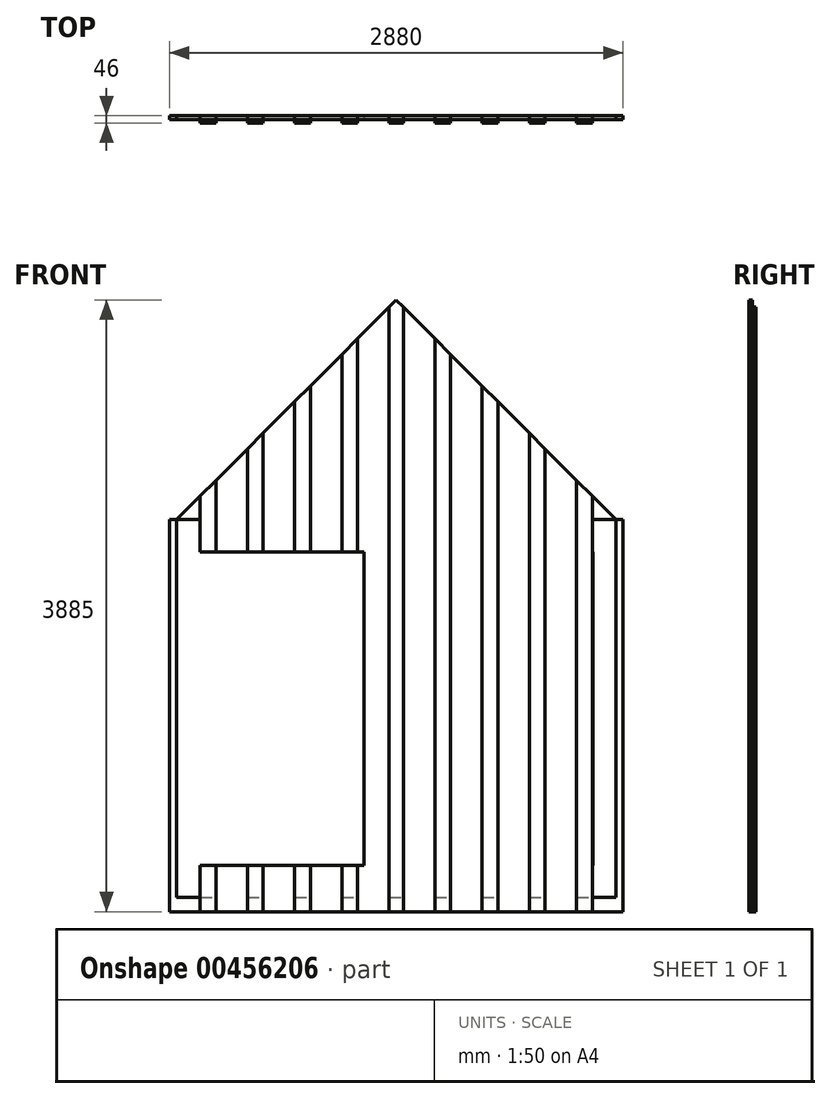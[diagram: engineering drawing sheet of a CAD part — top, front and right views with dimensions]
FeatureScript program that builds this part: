
annotation { "Feature Type Name" : "Feature", "Feature Type Description" : "" }
export const myFeature = defineFeature(function(context is Context, id is Id, definition is map)
    precondition{}
    {
        {
            var Q0;
            Q0=qCreatedBy(makeId("Front.planeOp"),FACE);
            var sketch = newSketch(context, id + "F0", { "sketchPlane" : qUnion([Q0])});
            skLineSegment(sketch, "E0.bottom", {"start": v(-2340, 1043.57) * mm, "end": v(450, 1043.57) * mm});
            skLineSegment(sketch, "E0.top", {"start": v(-2340, -1356.43) * mm, "end": v(450, -1356.43) * mm});
            skLineSegment(sketch, "E0.left", {"start": v(-2340, 1043.57) * mm, "end": v(-2340, -1356.43) * mm});
            skLineSegment(sketch, "E0.right", {"start": v(450, 1043.57) * mm, "end": v(450, -1356.43) * mm});
            skLineSegment(sketch, "E1", {"start": v(-2340, 1043.57) * mm, "end": v(-945, 2438.57) * mm});
            skPoint(sketch, "E1.endSnap0", {"position": v(-945, 1043.57) * mm});
            skLineSegment(sketch, "E2", {"start": v(-945, 2438.57) * mm, "end": v(450, 1043.57) * mm});
            skLineSegment(sketch, "E3.0", {"start": v(-945, 2233.5) * mm, "end": v(305, 983.5) * mm});
            skLineSegment(sketch, "E3.1", {"start": v(-2195, 983.5) * mm, "end": v(-945, 2233.5) * mm});
            skLineSegment(sketch, "E3.2", {"start": v(305, 983.5) * mm, "end": v(305, -1211.43) * mm});
            skLineSegment(sketch, "E3.3", {"start": v(-2195, -1211.43) * mm, "end": v(305, -1211.43) * mm});
            skLineSegment(sketch, "E3.4", {"start": v(-2195, 983.5) * mm, "end": v(-2195, -1211.43) * mm});
            skLineSegment(sketch, "E4.bottom", {"start": v(-2195, 983.5) * mm, "end": v(305, 983.5) * mm});
            skLineSegment(sketch, "E4.top", {"start": v(-2195, 838.5) * mm, "end": v(305, 838.5) * mm});
            skLineSegment(sketch, "E4.left", {"start": v(-2195, 983.5) * mm, "end": v(-2195, 838.5) * mm});
            skLineSegment(sketch, "E4.right", {"start": v(305, 983.5) * mm, "end": v(305, 838.5) * mm});
            skLineSegment(sketch, "E5", {"start": v(-2195, -1152) * mm, "end": v(305, -1152) * mm});
            skLineSegment(sketch, "E6", {"start": v(-2150, 838.5) * mm, "end": v(-2150, -1152) * mm});
            skLineSegment(sketch, "E7", {"start": v(260, 838.5) * mm, "end": v(260, -1152) * mm});
            skLineSegment(sketch, "E8.top", {"start": v(-2340, -1446.43) * mm, "end": v(450, -1446.43) * mm});
            skLineSegment(sketch, "E8.left", {"start": v(-2340, -1356.43) * mm, "end": v(-2340, -1446.43) * mm});
            skLineSegment(sketch, "E8.right", {"start": v(450, -1356.43) * mm, "end": v(450, -1446.43) * mm});
            skLineSegment(sketch, "E9", {"start": v(300, 988.5) * mm, "end": v(300, -1446.43) * mm});
            skLineSegment(sketch, "E10", {"start": v(200, 1088.5) * mm, "end": v(200, -1446.43) * mm});
            skLineSegment(sketch, "E11", {"start": v(0, 1288.5) * mm, "end": v(0, -1446.43) * mm});
            skLineSegment(sketch, "E12", {"start": v(-100, 1388.5) * mm, "end": v(-100, -1446.43) * mm});
            skLineSegment(sketch, "E13", {"start": v(-100, 1388.5) * mm, "end": v(-100, 1593.57) * mm});
            skLineSegment(sketch, "E14", {"start": v(0, 1288.5) * mm, "end": v(0, 1493.57) * mm});
            skLineSegment(sketch, "E15", {"start": v(200, 1088.5) * mm, "end": v(200, 1293.57) * mm});
            skLineSegment(sketch, "E16", {"start": v(300, 988.5) * mm, "end": v(300, 1193.57) * mm});
            skLineSegment(sketch, "E17", {"start": v(-300, 1793.57) * mm, "end": v(-300, -1446.43) * mm});
            skLineSegment(sketch, "E18", {"start": v(-400, 1893.57) * mm, "end": v(-400, -1446.43) * mm});
            skLineSegment(sketch, "E19", {"start": v(-600, 2093.57) * mm, "end": v(-600, -1446.43) * mm});
            skLineSegment(sketch, "E20", {"start": v(-700, 2193.57) * mm, "end": v(-700, -1446.43) * mm});
            skLineSegment(sketch, "E21", {"start": v(-900, 2393.57) * mm, "end": v(-900, -1446.43) * mm});
            skPoint(sketch, "E21.endSnap0", {"position": v(-945, -1446.43) * mm});
            skLineSegment(sketch, "E22", {"start": v(-945, 2438.57) * mm, "end": v(-945, 1939.82) * mm, "construction": true});
            skLineSegment(sketch, "E23.bottom", {"start": v(-2150, 838.5) * mm, "end": v(-1150, 838.5) * mm});
            skLineSegment(sketch, "E23.top", {"start": v(-2150, -1152) * mm, "end": v(-1150, -1152) * mm});
            skLineSegment(sketch, "E23.right", {"start": v(-1150, 838.5) * mm, "end": v(-1150, -1152) * mm});
            skLineSegment(sketch, "E24", {"start": v(-2150, 793.5) * mm, "end": v(-1150, 793.5) * mm});
            skLineSegment(sketch, "E25", {"start": v(-2150, -1107) * mm, "end": v(-1150, -1107) * mm});
            skLineSegment(sketch, "E26", {"start": v(-2105, 793.5) * mm, "end": v(-2105, -1107) * mm});
            skLineSegment(sketch, "E27", {"start": v(-1195, 793.5) * mm, "end": v(-1195, -1107) * mm});
            skLineSegment(sketch, "E28.MirrorCS", {"start": v(-2190, 988.5) * mm, "end": v(-2190, -1446.43) * mm});
            skLineSegment(sketch, "E29.MirrorCS", {"start": v(-2190, 988.5) * mm, "end": v(-2190, 1193.57) * mm});
            skLineSegment(sketch, "E30.MirrorCS", {"start": v(-2090, 1088.5) * mm, "end": v(-2090, -1446.43) * mm});
            skLineSegment(sketch, "E31.MirrorCS", {"start": v(-2090, 1088.5) * mm, "end": v(-2090, 1293.57) * mm});
            skLineSegment(sketch, "E32.MirrorCS", {"start": v(-1890, 1288.5) * mm, "end": v(-1890, 1493.57) * mm});
            skLineSegment(sketch, "E33.MirrorCS", {"start": v(-1790, 1388.5) * mm, "end": v(-1790, 1593.57) * mm});
            skLineSegment(sketch, "E34.MirrorCS", {"start": v(-1890, 1288.5) * mm, "end": v(-1890, -1446.43) * mm});
            skLineSegment(sketch, "E35.MirrorCS", {"start": v(-1790, 1388.5) * mm, "end": v(-1790, -1446.43) * mm});
            skLineSegment(sketch, "E36.MirrorCS", {"start": v(-1590, 1793.57) * mm, "end": v(-1590, -1446.43) * mm});
            skLineSegment(sketch, "E37.MirrorCS", {"start": v(-1490, 1893.57) * mm, "end": v(-1490, -1446.43) * mm});
            skLineSegment(sketch, "E38.MirrorCS", {"start": v(-1290, 2093.57) * mm, "end": v(-1290, -1446.43) * mm});
            skLineSegment(sketch, "E39.MirrorCS", {"start": v(-990, 2393.57) * mm, "end": v(-990, -1446.43) * mm});
            skLineSegment(sketch, "E40.MirrorCS", {"start": v(-1190, 2193.57) * mm, "end": v(-1190, -1446.43) * mm});
            skLineSegment(sketch, "E41.bottom", {"start": v(450, 1043.57) * mm, "end": v(495, 1043.57) * mm});
            skLineSegment(sketch, "E41.top", {"start": v(450, -1446.43) * mm, "end": v(495, -1446.43) * mm});
            skLineSegment(sketch, "E41.left", {"start": v(450, 1043.57) * mm, "end": v(450, -1446.43) * mm});
            skLineSegment(sketch, "E41.right", {"start": v(495, 1043.57) * mm, "end": v(495, -1446.43) * mm});
            skLineSegment(sketch, "E42.bottom", {"start": v(-2340, 1043.57) * mm, "end": v(-2385, 1043.57) * mm});
            skLineSegment(sketch, "E42.top", {"start": v(-2340, -1446.43) * mm, "end": v(-2385, -1446.43) * mm});
            skLineSegment(sketch, "E42.left", {"start": v(-2340, 1043.57) * mm, "end": v(-2340, -1446.43) * mm});
            skLineSegment(sketch, "E42.right", {"start": v(-2385, 1043.57) * mm, "end": v(-2385, -1446.43) * mm});
            skSolve(sketch);
        }
        {
            var Q0;
            {var subQ3=sQuery(id+"F0.wireOp",EDGE,"E41.bottom");Q0=makeQuery(id+"F0.imprint","IMPRINT",FACE,{"disambiguationData":[TD([[makeQuery(id+"F0.imprint","IMPRINT",EDGE,{"derivedFrom":subQ3}),-1.0]])]});}
            var Q1;
            {var subQ9=sQuery(id+"F0.wireOp",EDGE,"E4.right");Q1=makeQuery(id+"F0.imprint","IMPRINT",FACE,{"disambiguationData":[TD([[makeQuery(id+"F0.imprint","IMPRINT",EDGE,{"derivedFrom":subQ9}),1.0]])]});}
            var Q2;
            {var subQ1=sQuery(id+"F0.wireOp",EDGE,"E3.2");var subQ3=sQuery(id+"F0.wireOp",EDGE,"E5");var subQ4=makeQuery(id+"F0.imprint","INTERSECT",VERTEX,{"derivedFrom":[subQ1,subQ3]});Q2=makeQuery(id+"F0.imprint","IMPRINT",FACE,{"disambiguationData":[TD([[makeQuery(id+"F0.imprint","IMPRINT",EDGE,{"disambiguationData":[TD([[subQ4,1.0]])],"derivedFrom":subQ3}),1.0]])]});}
            var Q3;
            {var subQ0=sQuery(id+"F0.wireOp",EDGE,"E2");var subQ3=sQuery(id+"F0.wireOp",EDGE,"E16");var subQ5=makeQuery(id+"F0.imprint","INTERSECT",VERTEX,{"derivedFrom":[subQ0,subQ3]});Q3=makeQuery(id+"F0.imprint","IMPRINT",FACE,{"disambiguationData":[TD([[makeQuery(id+"F0.imprint","IMPRINT",EDGE,{"disambiguationData":[TD([[subQ5,1.0]])],"derivedFrom":subQ3}),-1.0]])]});}
            var Q4;
            {var subQ0=sQuery(id+"F0.wireOp",EDGE,"E14");Q4=makeQuery(id+"F0.imprint","IMPRINT",FACE,{"disambiguationData":[TD([[makeQuery(id+"F0.imprint","IMPRINT",EDGE,{"derivedFrom":subQ0}),-1.0]])]});}
            var Q5;
            {var subQ0=sQuery(id+"F0.wireOp",EDGE,"E11");var subQ1=sQuery(id+"F0.wireOp",EDGE,"E0.bottom");var subQ2=makeQuery(id+"F0.imprint","INTERSECT",VERTEX,{"derivedFrom":[subQ1,subQ0]});Q5=makeQuery(id+"F0.imprint","IMPRINT",FACE,{"disambiguationData":[TD([[makeQuery(id+"F0.imprint","IMPRINT",EDGE,{"disambiguationData":[TD([[subQ2,-1.0]])],"derivedFrom":subQ1}),1.0]])]});}
            var Q6;
            {var subQ0=sQuery(id+"F0.wireOp",EDGE,"E11");var subQ1=sQuery(id+"F0.wireOp",EDGE,"E0.bottom");var subQ2=makeQuery(id+"F0.imprint","INTERSECT",VERTEX,{"derivedFrom":[subQ1,subQ0]});Q6=makeQuery(id+"F0.imprint","IMPRINT",FACE,{"disambiguationData":[TD([[makeQuery(id+"F0.imprint","IMPRINT",EDGE,{"disambiguationData":[TD([[subQ2,-1.0]])],"derivedFrom":subQ1}),-1.0]])]});}
            var Q7;
            {var subQ0=sQuery(id+"F0.wireOp",EDGE,"E11");var subQ1=sQuery(id+"F0.wireOp",EDGE,"E4.bottom");var subQ2=makeQuery(id+"F0.imprint","INTERSECT",VERTEX,{"derivedFrom":[subQ1,subQ0]});Q7=makeQuery(id+"F0.imprint","IMPRINT",FACE,{"disambiguationData":[TD([[makeQuery(id+"F0.imprint","IMPRINT",EDGE,{"disambiguationData":[TD([[subQ2,-1.0]])],"derivedFrom":subQ1}),-1.0]])]});}
            var Q8;
            {var subQ0=sQuery(id+"F0.wireOp",EDGE,"E11");var subQ1=sQuery(id+"F0.wireOp",EDGE,"E4.top");var subQ2=makeQuery(id+"F0.imprint","INTERSECT",VERTEX,{"derivedFrom":[subQ1,subQ0]});Q8=makeQuery(id+"F0.imprint","IMPRINT",FACE,{"disambiguationData":[TD([[makeQuery(id+"F0.imprint","IMPRINT",EDGE,{"disambiguationData":[TD([[subQ2,-1.0]])],"derivedFrom":subQ1}),-1.0]])]});}
            var Q9;
            {var subQ0=sQuery(id+"F0.wireOp",EDGE,"E11");var subQ1=sQuery(id+"F0.wireOp",EDGE,"E3.3");var subQ2=makeQuery(id+"F0.imprint","INTERSECT",VERTEX,{"derivedFrom":[subQ1,subQ0]});Q9=makeQuery(id+"F0.imprint","IMPRINT",FACE,{"disambiguationData":[TD([[makeQuery(id+"F0.imprint","IMPRINT",EDGE,{"disambiguationData":[TD([[subQ2,-1.0]])],"derivedFrom":subQ1}),1.0]])]});}
            var Q10;
            {var subQ0=sQuery(id+"F0.wireOp",EDGE,"E11");var subQ1=sQuery(id+"F0.wireOp",EDGE,"E3.3");var subQ2=makeQuery(id+"F0.imprint","INTERSECT",VERTEX,{"derivedFrom":[subQ1,subQ0]});Q10=makeQuery(id+"F0.imprint","IMPRINT",FACE,{"disambiguationData":[TD([[makeQuery(id+"F0.imprint","IMPRINT",EDGE,{"disambiguationData":[TD([[subQ2,-1.0]])],"derivedFrom":subQ1}),-1.0]])]});}
            var Q11;
            {var subQ0=sQuery(id+"F0.wireOp",EDGE,"E11");var subQ1=sQuery(id+"F0.wireOp",EDGE,"E0.top");var subQ2=makeQuery(id+"F0.imprint","INTERSECT",VERTEX,{"derivedFrom":[subQ1,subQ0]});Q11=makeQuery(id+"F0.imprint","IMPRINT",FACE,{"disambiguationData":[TD([[makeQuery(id+"F0.imprint","IMPRINT",EDGE,{"disambiguationData":[TD([[subQ2,-1.0]])],"derivedFrom":subQ1}),-1.0]])]});}
            var Q12;
            {var subQ0=sQuery(id+"F0.wireOp",EDGE,"E17");var subQ1=sQuery(id+"F0.wireOp",EDGE,"E0.top");var subQ2=makeQuery(id+"F0.imprint","INTERSECT",VERTEX,{"derivedFrom":[subQ1,subQ0]});Q12=makeQuery(id+"F0.imprint","IMPRINT",FACE,{"disambiguationData":[TD([[makeQuery(id+"F0.imprint","IMPRINT",EDGE,{"disambiguationData":[TD([[subQ2,-1.0]])],"derivedFrom":subQ1}),-1.0]])]});}
            var Q13;
            {var subQ0=sQuery(id+"F0.wireOp",EDGE,"E17");var subQ1=sQuery(id+"F0.wireOp",EDGE,"E3.3");var subQ2=makeQuery(id+"F0.imprint","INTERSECT",VERTEX,{"derivedFrom":[subQ1,subQ0]});Q13=makeQuery(id+"F0.imprint","IMPRINT",FACE,{"disambiguationData":[TD([[makeQuery(id+"F0.imprint","IMPRINT",EDGE,{"disambiguationData":[TD([[subQ2,-1.0]])],"derivedFrom":subQ1}),-1.0]])]});}
            var Q14;
            {var subQ0=sQuery(id+"F0.wireOp",EDGE,"E17");var subQ1=sQuery(id+"F0.wireOp",EDGE,"E3.3");var subQ2=makeQuery(id+"F0.imprint","INTERSECT",VERTEX,{"derivedFrom":[subQ1,subQ0]});Q14=makeQuery(id+"F0.imprint","IMPRINT",FACE,{"disambiguationData":[TD([[makeQuery(id+"F0.imprint","IMPRINT",EDGE,{"disambiguationData":[TD([[subQ2,-1.0]])],"derivedFrom":subQ1}),1.0]])]});}
            var Q15;
            {var subQ0=sQuery(id+"F0.wireOp",EDGE,"E17");var subQ1=sQuery(id+"F0.wireOp",EDGE,"E4.top");var subQ2=makeQuery(id+"F0.imprint","INTERSECT",VERTEX,{"derivedFrom":[subQ1,subQ0]});Q15=makeQuery(id+"F0.imprint","IMPRINT",FACE,{"disambiguationData":[TD([[makeQuery(id+"F0.imprint","IMPRINT",EDGE,{"disambiguationData":[TD([[subQ2,-1.0]])],"derivedFrom":subQ1}),-1.0]])]});}
            var Q16;
            {var subQ0=sQuery(id+"F0.wireOp",EDGE,"E17");var subQ1=sQuery(id+"F0.wireOp",EDGE,"E4.bottom");var subQ2=makeQuery(id+"F0.imprint","INTERSECT",VERTEX,{"derivedFrom":[subQ1,subQ0]});Q16=makeQuery(id+"F0.imprint","IMPRINT",FACE,{"disambiguationData":[TD([[makeQuery(id+"F0.imprint","IMPRINT",EDGE,{"disambiguationData":[TD([[subQ2,-1.0]])],"derivedFrom":subQ1}),-1.0]])]});}
            var Q17;
            {var subQ0=sQuery(id+"F0.wireOp",EDGE,"E17");var subQ1=sQuery(id+"F0.wireOp",EDGE,"E0.bottom");var subQ2=makeQuery(id+"F0.imprint","INTERSECT",VERTEX,{"derivedFrom":[subQ1,subQ0]});Q17=makeQuery(id+"F0.imprint","IMPRINT",FACE,{"disambiguationData":[TD([[makeQuery(id+"F0.imprint","IMPRINT",EDGE,{"disambiguationData":[TD([[subQ2,-1.0]])],"derivedFrom":subQ1}),-1.0]])]});}
            var Q18;
            {var subQ0=sQuery(id+"F0.wireOp",EDGE,"E17");var subQ1=sQuery(id+"F0.wireOp",EDGE,"E0.bottom");var subQ2=makeQuery(id+"F0.imprint","INTERSECT",VERTEX,{"derivedFrom":[subQ1,subQ0]});Q18=makeQuery(id+"F0.imprint","IMPRINT",FACE,{"disambiguationData":[TD([[makeQuery(id+"F0.imprint","IMPRINT",EDGE,{"disambiguationData":[TD([[subQ2,-1.0]])],"derivedFrom":subQ1}),1.0]])]});}
            var Q19;
            {var subQ0=sQuery(id+"F0.wireOp",EDGE,"E13");Q19=makeQuery(id+"F0.imprint","IMPRINT",FACE,{"disambiguationData":[TD([[makeQuery(id+"F0.imprint","IMPRINT",EDGE,{"derivedFrom":subQ0}),1.0]])]});}
            var Q20;
            {var subQ0=sQuery(id+"F0.wireOp",EDGE,"E18");var subQ1=sQuery(id+"F0.wireOp",EDGE,"E2");var subQ2=makeQuery(id+"F0.imprint","INTERSECT",VERTEX,{"derivedFrom":[subQ1,subQ0]});Q20=makeQuery(id+"F0.imprint","IMPRINT",FACE,{"disambiguationData":[TD([[makeQuery(id+"F0.imprint","IMPRINT",EDGE,{"disambiguationData":[TD([[subQ2,1.0]])],"derivedFrom":subQ1}),-1.0]])]});}
            var Q21;
            {var subQ0=sQuery(id+"F0.wireOp",EDGE,"E19");var subQ1=sQuery(id+"F0.wireOp",EDGE,"E0.bottom");var subQ2=makeQuery(id+"F0.imprint","INTERSECT",VERTEX,{"derivedFrom":[subQ1,subQ0]});Q21=makeQuery(id+"F0.imprint","IMPRINT",FACE,{"disambiguationData":[TD([[makeQuery(id+"F0.imprint","IMPRINT",EDGE,{"disambiguationData":[TD([[subQ2,-1.0]])],"derivedFrom":subQ1}),1.0]])]});}
            var Q22;
            {var subQ0=sQuery(id+"F0.wireOp",EDGE,"E19");var subQ1=sQuery(id+"F0.wireOp",EDGE,"E0.bottom");var subQ2=makeQuery(id+"F0.imprint","INTERSECT",VERTEX,{"derivedFrom":[subQ1,subQ0]});Q22=makeQuery(id+"F0.imprint","IMPRINT",FACE,{"disambiguationData":[TD([[makeQuery(id+"F0.imprint","IMPRINT",EDGE,{"disambiguationData":[TD([[subQ2,-1.0]])],"derivedFrom":subQ1}),-1.0]])]});}
            var Q23;
            {var subQ0=sQuery(id+"F0.wireOp",EDGE,"E19");var subQ1=sQuery(id+"F0.wireOp",EDGE,"E4.bottom");var subQ2=makeQuery(id+"F0.imprint","INTERSECT",VERTEX,{"derivedFrom":[subQ1,subQ0]});Q23=makeQuery(id+"F0.imprint","IMPRINT",FACE,{"disambiguationData":[TD([[makeQuery(id+"F0.imprint","IMPRINT",EDGE,{"disambiguationData":[TD([[subQ2,-1.0]])],"derivedFrom":subQ1}),-1.0]])]});}
            var Q24;
            {var subQ0=sQuery(id+"F0.wireOp",EDGE,"E19");var subQ1=sQuery(id+"F0.wireOp",EDGE,"E4.top");var subQ2=makeQuery(id+"F0.imprint","INTERSECT",VERTEX,{"derivedFrom":[subQ1,subQ0]});Q24=makeQuery(id+"F0.imprint","IMPRINT",FACE,{"disambiguationData":[TD([[makeQuery(id+"F0.imprint","IMPRINT",EDGE,{"disambiguationData":[TD([[subQ2,-1.0]])],"derivedFrom":subQ1}),-1.0]])]});}
            var Q25;
            {var subQ0=sQuery(id+"F0.wireOp",EDGE,"E19");var subQ1=sQuery(id+"F0.wireOp",EDGE,"E3.3");var subQ2=makeQuery(id+"F0.imprint","INTERSECT",VERTEX,{"derivedFrom":[subQ1,subQ0]});Q25=makeQuery(id+"F0.imprint","IMPRINT",FACE,{"disambiguationData":[TD([[makeQuery(id+"F0.imprint","IMPRINT",EDGE,{"disambiguationData":[TD([[subQ2,-1.0]])],"derivedFrom":subQ1}),1.0]])]});}
            var Q26;
            {var subQ0=sQuery(id+"F0.wireOp",EDGE,"E19");var subQ1=sQuery(id+"F0.wireOp",EDGE,"E3.3");var subQ2=makeQuery(id+"F0.imprint","INTERSECT",VERTEX,{"derivedFrom":[subQ1,subQ0]});Q26=makeQuery(id+"F0.imprint","IMPRINT",FACE,{"disambiguationData":[TD([[makeQuery(id+"F0.imprint","IMPRINT",EDGE,{"disambiguationData":[TD([[subQ2,-1.0]])],"derivedFrom":subQ1}),-1.0]])]});}
            var Q27;
            {var subQ0=sQuery(id+"F0.wireOp",EDGE,"E19");var subQ1=sQuery(id+"F0.wireOp",EDGE,"E0.top");var subQ2=makeQuery(id+"F0.imprint","INTERSECT",VERTEX,{"derivedFrom":[subQ1,subQ0]});Q27=makeQuery(id+"F0.imprint","IMPRINT",FACE,{"disambiguationData":[TD([[makeQuery(id+"F0.imprint","IMPRINT",EDGE,{"disambiguationData":[TD([[subQ2,-1.0]])],"derivedFrom":subQ1}),-1.0]])]});}
            var Q28;
            {var subQ0=sQuery(id+"F0.wireOp",EDGE,"E21");var subQ1=sQuery(id+"F0.wireOp",EDGE,"E0.top");var subQ2=makeQuery(id+"F0.imprint","INTERSECT",VERTEX,{"derivedFrom":[subQ1,subQ0]});Q28=makeQuery(id+"F0.imprint","IMPRINT",FACE,{"disambiguationData":[TD([[makeQuery(id+"F0.imprint","IMPRINT",EDGE,{"disambiguationData":[TD([[subQ2,-1.0]])],"derivedFrom":subQ1}),-1.0]])]});}
            var Q29;
            {var subQ0=sQuery(id+"F0.wireOp",EDGE,"E21");var subQ1=sQuery(id+"F0.wireOp",EDGE,"E3.3");var subQ2=makeQuery(id+"F0.imprint","INTERSECT",VERTEX,{"derivedFrom":[subQ1,subQ0]});Q29=makeQuery(id+"F0.imprint","IMPRINT",FACE,{"disambiguationData":[TD([[makeQuery(id+"F0.imprint","IMPRINT",EDGE,{"disambiguationData":[TD([[subQ2,-1.0]])],"derivedFrom":subQ1}),-1.0]])]});}
            var Q30;
            {var subQ0=sQuery(id+"F0.wireOp",EDGE,"E21");var subQ1=sQuery(id+"F0.wireOp",EDGE,"E3.3");var subQ2=makeQuery(id+"F0.imprint","INTERSECT",VERTEX,{"derivedFrom":[subQ1,subQ0]});Q30=makeQuery(id+"F0.imprint","IMPRINT",FACE,{"disambiguationData":[TD([[makeQuery(id+"F0.imprint","IMPRINT",EDGE,{"disambiguationData":[TD([[subQ2,-1.0]])],"derivedFrom":subQ1}),1.0]])]});}
            var Q31;
            {var subQ0=sQuery(id+"F0.wireOp",EDGE,"E21");var subQ1=sQuery(id+"F0.wireOp",EDGE,"E4.top");var subQ2=makeQuery(id+"F0.imprint","INTERSECT",VERTEX,{"derivedFrom":[subQ1,subQ0]});Q31=makeQuery(id+"F0.imprint","IMPRINT",FACE,{"disambiguationData":[TD([[makeQuery(id+"F0.imprint","IMPRINT",EDGE,{"disambiguationData":[TD([[subQ2,-1.0]])],"derivedFrom":subQ1}),-1.0]])]});}
            var Q32;
            {var subQ0=sQuery(id+"F0.wireOp",EDGE,"E21");var subQ1=sQuery(id+"F0.wireOp",EDGE,"E4.bottom");var subQ2=makeQuery(id+"F0.imprint","INTERSECT",VERTEX,{"derivedFrom":[subQ1,subQ0]});Q32=makeQuery(id+"F0.imprint","IMPRINT",FACE,{"disambiguationData":[TD([[makeQuery(id+"F0.imprint","IMPRINT",EDGE,{"disambiguationData":[TD([[subQ2,-1.0]])],"derivedFrom":subQ1}),-1.0]])]});}
            var Q33;
            {var subQ0=sQuery(id+"F0.wireOp",EDGE,"E21");var subQ1=sQuery(id+"F0.wireOp",EDGE,"E0.bottom");var subQ2=makeQuery(id+"F0.imprint","INTERSECT",VERTEX,{"derivedFrom":[subQ1,subQ0]});Q33=makeQuery(id+"F0.imprint","IMPRINT",FACE,{"disambiguationData":[TD([[makeQuery(id+"F0.imprint","IMPRINT",EDGE,{"disambiguationData":[TD([[subQ2,-1.0]])],"derivedFrom":subQ1}),-1.0]])]});}
            var Q34;
            {var subQ0=sQuery(id+"F0.wireOp",EDGE,"E21");var subQ1=sQuery(id+"F0.wireOp",EDGE,"E0.bottom");var subQ2=makeQuery(id+"F0.imprint","INTERSECT",VERTEX,{"derivedFrom":[subQ1,subQ0]});Q34=makeQuery(id+"F0.imprint","IMPRINT",FACE,{"disambiguationData":[TD([[makeQuery(id+"F0.imprint","IMPRINT",EDGE,{"disambiguationData":[TD([[subQ2,-1.0]])],"derivedFrom":subQ1}),1.0]])]});}
            var Q35;
            {var subQ0=sQuery(id+"F0.wireOp",EDGE,"E20");var subQ1=sQuery(id+"F0.wireOp",EDGE,"E2");var subQ2=makeQuery(id+"F0.imprint","INTERSECT",VERTEX,{"derivedFrom":[subQ1,subQ0]});Q35=makeQuery(id+"F0.imprint","IMPRINT",FACE,{"disambiguationData":[TD([[makeQuery(id+"F0.imprint","IMPRINT",EDGE,{"disambiguationData":[TD([[subQ2,1.0]])],"derivedFrom":subQ1}),-1.0]])]});}
            var Q36;
            {var subQ0=sQuery(id+"F0.wireOp",EDGE,"E39.MirrorCS");var subQ1=sQuery(id+"F0.wireOp",EDGE,"E1");var subQ2=makeQuery(id+"F0.imprint","INTERSECT",VERTEX,{"derivedFrom":[subQ1,subQ0]});Q36=makeQuery(id+"F0.imprint","IMPRINT",FACE,{"disambiguationData":[TD([[makeQuery(id+"F0.imprint","IMPRINT",EDGE,{"disambiguationData":[TD([[subQ2,1.0]])],"derivedFrom":subQ1}),-1.0]])]});}
            var Q37;
            {var subQ0=sQuery(id+"F0.wireOp",EDGE,"E40.MirrorCS");var subQ1=sQuery(id+"F0.wireOp",EDGE,"E0.bottom");var subQ2=makeQuery(id+"F0.imprint","INTERSECT",VERTEX,{"derivedFrom":[subQ1,subQ0]});Q37=makeQuery(id+"F0.imprint","IMPRINT",FACE,{"disambiguationData":[TD([[makeQuery(id+"F0.imprint","IMPRINT",EDGE,{"disambiguationData":[TD([[subQ2,-1.0]])],"derivedFrom":subQ1}),1.0]])]});}
            var Q38;
            {var subQ0=sQuery(id+"F0.wireOp",EDGE,"E40.MirrorCS");var subQ1=sQuery(id+"F0.wireOp",EDGE,"E0.bottom");var subQ2=makeQuery(id+"F0.imprint","INTERSECT",VERTEX,{"derivedFrom":[subQ1,subQ0]});Q38=makeQuery(id+"F0.imprint","IMPRINT",FACE,{"disambiguationData":[TD([[makeQuery(id+"F0.imprint","IMPRINT",EDGE,{"disambiguationData":[TD([[subQ2,-1.0]])],"derivedFrom":subQ1}),-1.0]])]});}
            var Q39;
            {var subQ1=sQuery(id+"F0.wireOp",EDGE,"E4.bottom");var subQ7=sQuery(id+"F0.wireOp",EDGE,"E40.MirrorCS");var subQ9=makeQuery(id+"F0.imprint","INTERSECT",VERTEX,{"derivedFrom":[subQ1,subQ7]});Q39=makeQuery(id+"F0.imprint","IMPRINT",FACE,{"disambiguationData":[TD([[makeQuery(id+"F0.imprint","IMPRINT",EDGE,{"disambiguationData":[TD([[subQ9,-1.0]])],"derivedFrom":subQ1}),-1.0]])]});}
            var Q40;
            {var subQ0=sQuery(id+"F0.wireOp",EDGE,"E23.right");var subQ1=makeQuery(id+"F0.imprint","INTERSECT",VERTEX,{"derivedFrom":[subQ0,sQuery(id+"F0.wireOp",EDGE,"E24")]});Q40=makeQuery(id+"F0.imprint","IMPRINT",FACE,{"disambiguationData":[TD([[makeQuery(id+"F0.imprint","IMPRINT",EDGE,{"disambiguationData":[TD([[subQ1,-1.0]])],"derivedFrom":subQ0}),1.0]])]});}
            var Q41;
            {var subQ0=sQuery(id+"F0.wireOp",EDGE,"E40.MirrorCS");var subQ1=sQuery(id+"F0.wireOp",EDGE,"E3.3");var subQ2=makeQuery(id+"F0.imprint","INTERSECT",VERTEX,{"derivedFrom":[subQ1,subQ0]});Q41=makeQuery(id+"F0.imprint","IMPRINT",FACE,{"disambiguationData":[TD([[makeQuery(id+"F0.imprint","IMPRINT",EDGE,{"disambiguationData":[TD([[subQ2,-1.0]])],"derivedFrom":subQ1}),-1.0]])]});}
            var Q42;
            {var subQ3=sQuery(id+"F0.wireOp",EDGE,"E40.MirrorCS");var subQ6=sQuery(id+"F0.wireOp",EDGE,"E3.3");var subQ9=makeQuery(id+"F0.imprint","INTERSECT",VERTEX,{"derivedFrom":[subQ6,subQ3]});Q42=makeQuery(id+"F0.imprint","IMPRINT",FACE,{"disambiguationData":[TD([[makeQuery(id+"F0.imprint","IMPRINT",EDGE,{"disambiguationData":[TD([[subQ9,-1.0]])],"derivedFrom":subQ6}),1.0]])]});}
            var Q43;
            {var subQ0=sQuery(id+"F0.wireOp",EDGE,"E37.MirrorCS");var subQ1=sQuery(id+"F0.wireOp",EDGE,"E3.3");var subQ2=makeQuery(id+"F0.imprint","INTERSECT",VERTEX,{"derivedFrom":[subQ1,subQ0]});Q43=makeQuery(id+"F0.imprint","IMPRINT",FACE,{"disambiguationData":[TD([[makeQuery(id+"F0.imprint","IMPRINT",EDGE,{"disambiguationData":[TD([[subQ2,-1.0]])],"derivedFrom":subQ1}),-1.0]])]});}
            var Q44;
            {var subQ0=sQuery(id+"F0.wireOp",EDGE,"E37.MirrorCS");var subQ1=sQuery(id+"F0.wireOp",EDGE,"E3.3");var subQ2=makeQuery(id+"F0.imprint","INTERSECT",VERTEX,{"derivedFrom":[subQ1,subQ0]});Q44=makeQuery(id+"F0.imprint","IMPRINT",FACE,{"disambiguationData":[TD([[makeQuery(id+"F0.imprint","IMPRINT",EDGE,{"disambiguationData":[TD([[subQ2,-1.0]])],"derivedFrom":subQ1}),1.0]])]});}
            var Q45;
            {var subQ0=sQuery(id+"F0.wireOp",EDGE,"E40.MirrorCS");var subQ1=sQuery(id+"F0.wireOp",EDGE,"E0.top");var subQ2=makeQuery(id+"F0.imprint","INTERSECT",VERTEX,{"derivedFrom":[subQ1,subQ0]});Q45=makeQuery(id+"F0.imprint","IMPRINT",FACE,{"disambiguationData":[TD([[makeQuery(id+"F0.imprint","IMPRINT",EDGE,{"disambiguationData":[TD([[subQ2,-1.0]])],"derivedFrom":subQ1}),-1.0]])]});}
            var Q46;
            {var subQ0=sQuery(id+"F0.wireOp",EDGE,"E37.MirrorCS");var subQ1=sQuery(id+"F0.wireOp",EDGE,"E0.top");var subQ2=makeQuery(id+"F0.imprint","INTERSECT",VERTEX,{"derivedFrom":[subQ1,subQ0]});Q46=makeQuery(id+"F0.imprint","IMPRINT",FACE,{"disambiguationData":[TD([[makeQuery(id+"F0.imprint","IMPRINT",EDGE,{"disambiguationData":[TD([[subQ2,-1.0]])],"derivedFrom":subQ1}),-1.0]])]});}
            var Q47;
            {var subQ0=sQuery(id+"F0.wireOp",EDGE,"E35.MirrorCS");var subQ1=sQuery(id+"F0.wireOp",EDGE,"E0.top");var subQ2=makeQuery(id+"F0.imprint","INTERSECT",VERTEX,{"derivedFrom":[subQ1,subQ0]});Q47=makeQuery(id+"F0.imprint","IMPRINT",FACE,{"disambiguationData":[TD([[makeQuery(id+"F0.imprint","IMPRINT",EDGE,{"disambiguationData":[TD([[subQ2,-1.0]])],"derivedFrom":subQ1}),-1.0]])]});}
            var Q48;
            {var subQ0=sQuery(id+"F0.wireOp",EDGE,"E35.MirrorCS");var subQ1=sQuery(id+"F0.wireOp",EDGE,"E3.3");var subQ2=makeQuery(id+"F0.imprint","INTERSECT",VERTEX,{"derivedFrom":[subQ1,subQ0]});Q48=makeQuery(id+"F0.imprint","IMPRINT",FACE,{"disambiguationData":[TD([[makeQuery(id+"F0.imprint","IMPRINT",EDGE,{"disambiguationData":[TD([[subQ2,-1.0]])],"derivedFrom":subQ1}),-1.0]])]});}
            var Q49;
            {var subQ0=sQuery(id+"F0.wireOp",EDGE,"E35.MirrorCS");var subQ1=sQuery(id+"F0.wireOp",EDGE,"E3.3");var subQ2=makeQuery(id+"F0.imprint","INTERSECT",VERTEX,{"derivedFrom":[subQ1,subQ0]});Q49=makeQuery(id+"F0.imprint","IMPRINT",FACE,{"disambiguationData":[TD([[makeQuery(id+"F0.imprint","IMPRINT",EDGE,{"disambiguationData":[TD([[subQ2,-1.0]])],"derivedFrom":subQ1}),1.0]])]});}
            var Q50;
            {var subQ0=sQuery(id+"F0.wireOp",EDGE,"E30.MirrorCS");var subQ1=sQuery(id+"F0.wireOp",EDGE,"E0.top");var subQ2=makeQuery(id+"F0.imprint","INTERSECT",VERTEX,{"derivedFrom":[subQ1,subQ0]});Q50=makeQuery(id+"F0.imprint","IMPRINT",FACE,{"disambiguationData":[TD([[makeQuery(id+"F0.imprint","IMPRINT",EDGE,{"disambiguationData":[TD([[subQ2,-1.0]])],"derivedFrom":subQ1}),-1.0]])]});}
            var Q51;
            {var subQ0=sQuery(id+"F0.wireOp",EDGE,"E30.MirrorCS");var subQ1=sQuery(id+"F0.wireOp",EDGE,"E3.3");var subQ2=makeQuery(id+"F0.imprint","INTERSECT",VERTEX,{"derivedFrom":[subQ1,subQ0]});Q51=makeQuery(id+"F0.imprint","IMPRINT",FACE,{"disambiguationData":[TD([[makeQuery(id+"F0.imprint","IMPRINT",EDGE,{"disambiguationData":[TD([[subQ2,-1.0]])],"derivedFrom":subQ1}),-1.0]])]});}
            var Q52;
            {var subQ0=sQuery(id+"F0.wireOp",EDGE,"E30.MirrorCS");var subQ1=sQuery(id+"F0.wireOp",EDGE,"E3.3");var subQ2=makeQuery(id+"F0.imprint","INTERSECT",VERTEX,{"derivedFrom":[subQ1,subQ0]});Q52=makeQuery(id+"F0.imprint","IMPRINT",FACE,{"disambiguationData":[TD([[makeQuery(id+"F0.imprint","IMPRINT",EDGE,{"disambiguationData":[TD([[subQ2,-1.0]])],"derivedFrom":subQ1}),1.0]])]});}
            var Q53;
            {var subQ0=sQuery(id+"F0.wireOp",EDGE,"E42.left");var subQ1=sQuery(id+"F0.wireOp",EDGE,"E0.top");var subQ2=makeQuery(id+"F0.imprint","INTERSECT",VERTEX,{"derivedFrom":[subQ1,subQ0]});Q53=makeQuery(id+"F0.imprint","IMPRINT",FACE,{"disambiguationData":[TD([[makeQuery(id+"F0.imprint","IMPRINT",EDGE,{"disambiguationData":[TD([[subQ2,-1.0]])],"derivedFrom":subQ1}),-1.0]])]});}
            var Q54;
            {var subQ3=sQuery(id+"F0.wireOp",EDGE,"E42.bottom");Q54=makeQuery(id+"F0.imprint","IMPRINT",FACE,{"disambiguationData":[TD([[makeQuery(id+"F0.imprint","IMPRINT",EDGE,{"derivedFrom":subQ3}),1.0]])]});}
            var Q55;
            {var subQ0=sQuery(id+"F0.wireOp",EDGE,"E4.left");Q55=makeQuery(id+"F0.imprint","IMPRINT",FACE,{"disambiguationData":[TD([[makeQuery(id+"F0.imprint","IMPRINT",EDGE,{"derivedFrom":subQ0}),-1.0]])]});}
            var Q56;
            {var subQ0=sQuery(id+"F0.wireOp",EDGE,"E1");var subQ3=sQuery(id+"F0.wireOp",EDGE,"E29.MirrorCS");var subQ5=makeQuery(id+"F0.imprint","INTERSECT",VERTEX,{"derivedFrom":[subQ0,subQ3]});Q56=makeQuery(id+"F0.imprint","IMPRINT",FACE,{"disambiguationData":[TD([[makeQuery(id+"F0.imprint","IMPRINT",EDGE,{"disambiguationData":[TD([[subQ5,1.0]])],"derivedFrom":subQ3}),1.0]])]});}
            var Q57;
            {var subQ0=sQuery(id+"F0.wireOp",EDGE,"E31.MirrorCS");Q57=makeQuery(id+"F0.imprint","IMPRINT",FACE,{"disambiguationData":[TD([[makeQuery(id+"F0.imprint","IMPRINT",EDGE,{"derivedFrom":subQ0}),-1.0]])]});}
            var Q58;
            {var subQ0=sQuery(id+"F0.wireOp",EDGE,"E30.MirrorCS");var subQ1=sQuery(id+"F0.wireOp",EDGE,"E0.bottom");var subQ2=makeQuery(id+"F0.imprint","INTERSECT",VERTEX,{"derivedFrom":[subQ1,subQ0]});Q58=makeQuery(id+"F0.imprint","IMPRINT",FACE,{"disambiguationData":[TD([[makeQuery(id+"F0.imprint","IMPRINT",EDGE,{"disambiguationData":[TD([[subQ2,-1.0]])],"derivedFrom":subQ1}),1.0]])]});}
            var Q59;
            {var subQ0=sQuery(id+"F0.wireOp",EDGE,"E35.MirrorCS");var subQ1=sQuery(id+"F0.wireOp",EDGE,"E0.bottom");var subQ2=makeQuery(id+"F0.imprint","INTERSECT",VERTEX,{"derivedFrom":[subQ1,subQ0]});Q59=makeQuery(id+"F0.imprint","IMPRINT",FACE,{"disambiguationData":[TD([[makeQuery(id+"F0.imprint","IMPRINT",EDGE,{"disambiguationData":[TD([[subQ2,-1.0]])],"derivedFrom":subQ1}),1.0]])]});}
            var Q60;
            {var subQ0=sQuery(id+"F0.wireOp",EDGE,"E33.MirrorCS");Q60=makeQuery(id+"F0.imprint","IMPRINT",FACE,{"disambiguationData":[TD([[makeQuery(id+"F0.imprint","IMPRINT",EDGE,{"derivedFrom":subQ0}),-1.0]])]});}
            var Q61;
            {var subQ0=sQuery(id+"F0.wireOp",EDGE,"E37.MirrorCS");var subQ1=sQuery(id+"F0.wireOp",EDGE,"E0.bottom");var subQ2=makeQuery(id+"F0.imprint","INTERSECT",VERTEX,{"derivedFrom":[subQ1,subQ0]});Q61=makeQuery(id+"F0.imprint","IMPRINT",FACE,{"disambiguationData":[TD([[makeQuery(id+"F0.imprint","IMPRINT",EDGE,{"disambiguationData":[TD([[subQ2,-1.0]])],"derivedFrom":subQ1}),1.0]])]});}
            var Q62;
            {var subQ0=sQuery(id+"F0.wireOp",EDGE,"E37.MirrorCS");var subQ1=sQuery(id+"F0.wireOp",EDGE,"E1");var subQ2=makeQuery(id+"F0.imprint","INTERSECT",VERTEX,{"derivedFrom":[subQ1,subQ0]});Q62=makeQuery(id+"F0.imprint","IMPRINT",FACE,{"disambiguationData":[TD([[makeQuery(id+"F0.imprint","IMPRINT",EDGE,{"disambiguationData":[TD([[subQ2,-1.0]])],"derivedFrom":subQ1}),-1.0]])]});}
            var Q63;
            {var subQ0=sQuery(id+"F0.wireOp",EDGE,"E30.MirrorCS");var subQ1=sQuery(id+"F0.wireOp",EDGE,"E0.bottom");var subQ2=makeQuery(id+"F0.imprint","INTERSECT",VERTEX,{"derivedFrom":[subQ1,subQ0]});Q63=makeQuery(id+"F0.imprint","IMPRINT",FACE,{"disambiguationData":[TD([[makeQuery(id+"F0.imprint","IMPRINT",EDGE,{"disambiguationData":[TD([[subQ2,-1.0]])],"derivedFrom":subQ1}),-1.0]])]});}
            var Q64;
            {var subQ0=sQuery(id+"F0.wireOp",EDGE,"E30.MirrorCS");var subQ1=sQuery(id+"F0.wireOp",EDGE,"E4.bottom");var subQ2=makeQuery(id+"F0.imprint","INTERSECT",VERTEX,{"derivedFrom":[subQ1,subQ0]});Q64=makeQuery(id+"F0.imprint","IMPRINT",FACE,{"disambiguationData":[TD([[makeQuery(id+"F0.imprint","IMPRINT",EDGE,{"disambiguationData":[TD([[subQ2,-1.0]])],"derivedFrom":subQ1}),-1.0]])]});}
            var Q65;
            {var subQ0=sQuery(id+"F0.wireOp",EDGE,"E35.MirrorCS");var subQ1=sQuery(id+"F0.wireOp",EDGE,"E0.bottom");var subQ2=makeQuery(id+"F0.imprint","INTERSECT",VERTEX,{"derivedFrom":[subQ1,subQ0]});Q65=makeQuery(id+"F0.imprint","IMPRINT",FACE,{"disambiguationData":[TD([[makeQuery(id+"F0.imprint","IMPRINT",EDGE,{"disambiguationData":[TD([[subQ2,-1.0]])],"derivedFrom":subQ1}),-1.0]])]});}
            var Q66;
            {var subQ0=sQuery(id+"F0.wireOp",EDGE,"E35.MirrorCS");var subQ1=sQuery(id+"F0.wireOp",EDGE,"E4.bottom");var subQ2=makeQuery(id+"F0.imprint","INTERSECT",VERTEX,{"derivedFrom":[subQ1,subQ0]});Q66=makeQuery(id+"F0.imprint","IMPRINT",FACE,{"disambiguationData":[TD([[makeQuery(id+"F0.imprint","IMPRINT",EDGE,{"disambiguationData":[TD([[subQ2,-1.0]])],"derivedFrom":subQ1}),-1.0]])]});}
            var Q67;
            {var subQ0=sQuery(id+"F0.wireOp",EDGE,"E37.MirrorCS");var subQ1=sQuery(id+"F0.wireOp",EDGE,"E0.bottom");var subQ2=makeQuery(id+"F0.imprint","INTERSECT",VERTEX,{"derivedFrom":[subQ1,subQ0]});Q67=makeQuery(id+"F0.imprint","IMPRINT",FACE,{"disambiguationData":[TD([[makeQuery(id+"F0.imprint","IMPRINT",EDGE,{"disambiguationData":[TD([[subQ2,-1.0]])],"derivedFrom":subQ1}),-1.0]])]});}
            var Q68;
            {var subQ0=sQuery(id+"F0.wireOp",EDGE,"E37.MirrorCS");var subQ1=sQuery(id+"F0.wireOp",EDGE,"E4.bottom");var subQ2=makeQuery(id+"F0.imprint","INTERSECT",VERTEX,{"derivedFrom":[subQ1,subQ0]});Q68=makeQuery(id+"F0.imprint","IMPRINT",FACE,{"disambiguationData":[TD([[makeQuery(id+"F0.imprint","IMPRINT",EDGE,{"disambiguationData":[TD([[subQ2,-1.0]])],"derivedFrom":subQ1}),-1.0]])]});}
            var Q69;
            {var subQ0=sQuery(id+"F0.wireOp",EDGE,"E41.left");var subQ1=sQuery(id+"F0.wireOp",EDGE,"E0.top");var subQ2=makeQuery(id+"F0.imprint","INTERSECT",VERTEX,{"derivedFrom":[subQ1,subQ0]});Q69=makeQuery(id+"F0.imprint","IMPRINT",FACE,{"disambiguationData":[TD([[makeQuery(id+"F0.imprint","IMPRINT",EDGE,{"disambiguationData":[TD([[subQ2,1.0]])],"derivedFrom":subQ1}),-1.0]])]});}
            extrude(context, id + "F1", {"entities" : qUnion([Q0, Q1, Q2, Q3, Q4, Q5, Q6, Q7, Q8, Q9, Q10, Q11, Q12, Q13, Q14, Q15, Q16, Q17, Q18, Q19, Q20, Q21, Q22, Q23, Q24, Q25, Q26, Q27, Q28, Q29, Q30, Q31, Q32, Q33, Q34, Q35, Q36, Q37, Q38, Q39, Q40, Q41, Q42, Q43, Q44, Q45, Q46, Q47, Q48, Q49, Q50, Q51, Q52, Q53, Q54, Q55, Q56, Q57, Q58, Q59, Q60, Q61, Q62, Q63, Q64, Q65, Q66, Q67, Q68, Q69]), "depth" : -23 * mm, "offsetDistance" : 25 * mm});
        }
        {
            var Q0;
            {var subQ0=sQuery(id+"F0.wireOp",EDGE,"E15");Q0=makeQuery(id+"F0.imprint","IMPRINT",FACE,{"disambiguationData":[TD([[makeQuery(id+"F0.imprint","IMPRINT",EDGE,{"derivedFrom":subQ0}),-1.0]])]});}
            var Q1;
            {var subQ5=sQuery(id+"F0.wireOp",EDGE,"E0.bottom");var subQ7=sQuery(id+"F0.wireOp",EDGE,"E10");var subQ9=makeQuery(id+"F0.imprint","INTERSECT",VERTEX,{"derivedFrom":[subQ5,subQ7]});Q1=makeQuery(id+"F0.imprint","IMPRINT",FACE,{"disambiguationData":[TD([[makeQuery(id+"F0.imprint","IMPRINT",EDGE,{"disambiguationData":[TD([[subQ9,-1.0]])],"derivedFrom":subQ5}),-1.0]])]});}
            var Q2;
            {var subQ0=sQuery(id+"F0.wireOp",EDGE,"E10");var subQ1=sQuery(id+"F0.wireOp",EDGE,"E0.bottom");var subQ2=makeQuery(id+"F0.imprint","INTERSECT",VERTEX,{"derivedFrom":[subQ1,subQ0]});Q2=makeQuery(id+"F0.imprint","IMPRINT",FACE,{"disambiguationData":[TD([[makeQuery(id+"F0.imprint","IMPRINT",EDGE,{"disambiguationData":[TD([[subQ2,-1.0]])],"derivedFrom":subQ1}),1.0]])]});}
            var Q3;
            {var subQ0=sQuery(id+"F0.wireOp",EDGE,"E3.0");var subQ1=sQuery(id+"F0.wireOp",EDGE,"E0.bottom");var subQ2=makeQuery(id+"F0.imprint","INTERSECT",VERTEX,{"derivedFrom":[subQ1,subQ0]});Q3=makeQuery(id+"F0.imprint","IMPRINT",FACE,{"disambiguationData":[TD([[makeQuery(id+"F0.imprint","IMPRINT",EDGE,{"disambiguationData":[TD([[subQ2,-1.0]])],"derivedFrom":subQ1}),-1.0]])]});}
            var Q4;
            {var subQ1=sQuery(id+"F0.wireOp",EDGE,"E4.bottom");var subQ6=sQuery(id+"F0.wireOp",EDGE,"E10");var subQ8=makeQuery(id+"F0.imprint","INTERSECT",VERTEX,{"derivedFrom":[subQ1,subQ6]});Q4=makeQuery(id+"F0.imprint","IMPRINT",FACE,{"disambiguationData":[TD([[makeQuery(id+"F0.imprint","IMPRINT",EDGE,{"disambiguationData":[TD([[subQ8,-1.0]])],"derivedFrom":subQ1}),-1.0]])]});}
            var Q5;
            {var subQ0=sQuery(id+"F0.wireOp",EDGE,"E7");Q5=makeQuery(id+"F0.imprint","IMPRINT",FACE,{"disambiguationData":[TD([[makeQuery(id+"F0.imprint","IMPRINT",EDGE,{"derivedFrom":subQ0}),-1.0]])]});}
            var Q6;
            {var subQ0=sQuery(id+"F0.wireOp",EDGE,"E7");Q6=makeQuery(id+"F0.imprint","IMPRINT",FACE,{"disambiguationData":[TD([[makeQuery(id+"F0.imprint","IMPRINT",EDGE,{"derivedFrom":subQ0}),1.0]])]});}
            var Q7;
            {var subQ4=sQuery(id+"F0.wireOp",EDGE,"E3.3");var subQ6=sQuery(id+"F0.wireOp",EDGE,"E10");var subQ8=makeQuery(id+"F0.imprint","INTERSECT",VERTEX,{"derivedFrom":[subQ4,subQ6]});Q7=makeQuery(id+"F0.imprint","IMPRINT",FACE,{"disambiguationData":[TD([[makeQuery(id+"F0.imprint","IMPRINT",EDGE,{"disambiguationData":[TD([[subQ8,-1.0]])],"derivedFrom":subQ4}),1.0]])]});}
            var Q8;
            {var subQ0=sQuery(id+"F0.wireOp",EDGE,"E10");var subQ1=sQuery(id+"F0.wireOp",EDGE,"E3.3");var subQ2=makeQuery(id+"F0.imprint","INTERSECT",VERTEX,{"derivedFrom":[subQ1,subQ0]});Q8=makeQuery(id+"F0.imprint","IMPRINT",FACE,{"disambiguationData":[TD([[makeQuery(id+"F0.imprint","IMPRINT",EDGE,{"disambiguationData":[TD([[subQ2,-1.0]])],"derivedFrom":subQ1}),-1.0]])]});}
            var Q9;
            {var subQ0=sQuery(id+"F0.wireOp",EDGE,"E10");var subQ1=sQuery(id+"F0.wireOp",EDGE,"E0.top");var subQ2=makeQuery(id+"F0.imprint","INTERSECT",VERTEX,{"derivedFrom":[subQ1,subQ0]});Q9=makeQuery(id+"F0.imprint","IMPRINT",FACE,{"disambiguationData":[TD([[makeQuery(id+"F0.imprint","IMPRINT",EDGE,{"disambiguationData":[TD([[subQ2,-1.0]])],"derivedFrom":subQ1}),-1.0]])]});}
            var Q10;
            {var subQ0=sQuery(id+"F0.wireOp",EDGE,"E12");var subQ1=sQuery(id+"F0.wireOp",EDGE,"E0.top");var subQ2=makeQuery(id+"F0.imprint","INTERSECT",VERTEX,{"derivedFrom":[subQ1,subQ0]});Q10=makeQuery(id+"F0.imprint","IMPRINT",FACE,{"disambiguationData":[TD([[makeQuery(id+"F0.imprint","IMPRINT",EDGE,{"disambiguationData":[TD([[subQ2,-1.0]])],"derivedFrom":subQ1}),-1.0]])]});}
            var Q11;
            {var subQ0=sQuery(id+"F0.wireOp",EDGE,"E12");var subQ1=sQuery(id+"F0.wireOp",EDGE,"E3.3");var subQ2=makeQuery(id+"F0.imprint","INTERSECT",VERTEX,{"derivedFrom":[subQ1,subQ0]});Q11=makeQuery(id+"F0.imprint","IMPRINT",FACE,{"disambiguationData":[TD([[makeQuery(id+"F0.imprint","IMPRINT",EDGE,{"disambiguationData":[TD([[subQ2,-1.0]])],"derivedFrom":subQ1}),-1.0]])]});}
            var Q12;
            {var subQ0=sQuery(id+"F0.wireOp",EDGE,"E12");var subQ1=sQuery(id+"F0.wireOp",EDGE,"E3.3");var subQ2=makeQuery(id+"F0.imprint","INTERSECT",VERTEX,{"derivedFrom":[subQ1,subQ0]});Q12=makeQuery(id+"F0.imprint","IMPRINT",FACE,{"disambiguationData":[TD([[makeQuery(id+"F0.imprint","IMPRINT",EDGE,{"disambiguationData":[TD([[subQ2,-1.0]])],"derivedFrom":subQ1}),1.0]])]});}
            var Q13;
            {var subQ0=sQuery(id+"F0.wireOp",EDGE,"E12");var subQ1=sQuery(id+"F0.wireOp",EDGE,"E4.top");var subQ2=makeQuery(id+"F0.imprint","INTERSECT",VERTEX,{"derivedFrom":[subQ1,subQ0]});Q13=makeQuery(id+"F0.imprint","IMPRINT",FACE,{"disambiguationData":[TD([[makeQuery(id+"F0.imprint","IMPRINT",EDGE,{"disambiguationData":[TD([[subQ2,-1.0]])],"derivedFrom":subQ1}),-1.0]])]});}
            var Q14;
            {var subQ0=sQuery(id+"F0.wireOp",EDGE,"E12");var subQ1=sQuery(id+"F0.wireOp",EDGE,"E4.bottom");var subQ2=makeQuery(id+"F0.imprint","INTERSECT",VERTEX,{"derivedFrom":[subQ1,subQ0]});Q14=makeQuery(id+"F0.imprint","IMPRINT",FACE,{"disambiguationData":[TD([[makeQuery(id+"F0.imprint","IMPRINT",EDGE,{"disambiguationData":[TD([[subQ2,-1.0]])],"derivedFrom":subQ1}),-1.0]])]});}
            var Q15;
            {var subQ0=sQuery(id+"F0.wireOp",EDGE,"E12");var subQ1=sQuery(id+"F0.wireOp",EDGE,"E0.bottom");var subQ2=makeQuery(id+"F0.imprint","INTERSECT",VERTEX,{"derivedFrom":[subQ1,subQ0]});Q15=makeQuery(id+"F0.imprint","IMPRINT",FACE,{"disambiguationData":[TD([[makeQuery(id+"F0.imprint","IMPRINT",EDGE,{"disambiguationData":[TD([[subQ2,-1.0]])],"derivedFrom":subQ1}),-1.0]])]});}
            var Q16;
            {var subQ0=sQuery(id+"F0.wireOp",EDGE,"E12");var subQ1=sQuery(id+"F0.wireOp",EDGE,"E0.bottom");var subQ2=makeQuery(id+"F0.imprint","INTERSECT",VERTEX,{"derivedFrom":[subQ1,subQ0]});Q16=makeQuery(id+"F0.imprint","IMPRINT",FACE,{"disambiguationData":[TD([[makeQuery(id+"F0.imprint","IMPRINT",EDGE,{"disambiguationData":[TD([[subQ2,-1.0]])],"derivedFrom":subQ1}),1.0]])]});}
            var Q17;
            {var subQ0=sQuery(id+"F0.wireOp",EDGE,"E13");Q17=makeQuery(id+"F0.imprint","IMPRINT",FACE,{"disambiguationData":[TD([[makeQuery(id+"F0.imprint","IMPRINT",EDGE,{"derivedFrom":subQ0}),-1.0]])]});}
            var Q18;
            {var subQ0=sQuery(id+"F0.wireOp",EDGE,"E17");var subQ1=sQuery(id+"F0.wireOp",EDGE,"E2");var subQ2=makeQuery(id+"F0.imprint","INTERSECT",VERTEX,{"derivedFrom":[subQ1,subQ0]});Q18=makeQuery(id+"F0.imprint","IMPRINT",FACE,{"disambiguationData":[TD([[makeQuery(id+"F0.imprint","IMPRINT",EDGE,{"disambiguationData":[TD([[subQ2,1.0]])],"derivedFrom":subQ1}),-1.0]])]});}
            var Q19;
            {var subQ0=sQuery(id+"F0.wireOp",EDGE,"E18");var subQ1=sQuery(id+"F0.wireOp",EDGE,"E0.bottom");var subQ2=makeQuery(id+"F0.imprint","INTERSECT",VERTEX,{"derivedFrom":[subQ1,subQ0]});Q19=makeQuery(id+"F0.imprint","IMPRINT",FACE,{"disambiguationData":[TD([[makeQuery(id+"F0.imprint","IMPRINT",EDGE,{"disambiguationData":[TD([[subQ2,-1.0]])],"derivedFrom":subQ1}),1.0]])]});}
            var Q20;
            {var subQ0=sQuery(id+"F0.wireOp",EDGE,"E18");var subQ1=sQuery(id+"F0.wireOp",EDGE,"E0.bottom");var subQ2=makeQuery(id+"F0.imprint","INTERSECT",VERTEX,{"derivedFrom":[subQ1,subQ0]});Q20=makeQuery(id+"F0.imprint","IMPRINT",FACE,{"disambiguationData":[TD([[makeQuery(id+"F0.imprint","IMPRINT",EDGE,{"disambiguationData":[TD([[subQ2,-1.0]])],"derivedFrom":subQ1}),-1.0]])]});}
            var Q21;
            {var subQ0=sQuery(id+"F0.wireOp",EDGE,"E18");var subQ1=sQuery(id+"F0.wireOp",EDGE,"E4.bottom");var subQ2=makeQuery(id+"F0.imprint","INTERSECT",VERTEX,{"derivedFrom":[subQ1,subQ0]});Q21=makeQuery(id+"F0.imprint","IMPRINT",FACE,{"disambiguationData":[TD([[makeQuery(id+"F0.imprint","IMPRINT",EDGE,{"disambiguationData":[TD([[subQ2,-1.0]])],"derivedFrom":subQ1}),-1.0]])]});}
            var Q22;
            {var subQ0=sQuery(id+"F0.wireOp",EDGE,"E18");var subQ1=sQuery(id+"F0.wireOp",EDGE,"E4.top");var subQ2=makeQuery(id+"F0.imprint","INTERSECT",VERTEX,{"derivedFrom":[subQ1,subQ0]});Q22=makeQuery(id+"F0.imprint","IMPRINT",FACE,{"disambiguationData":[TD([[makeQuery(id+"F0.imprint","IMPRINT",EDGE,{"disambiguationData":[TD([[subQ2,-1.0]])],"derivedFrom":subQ1}),-1.0]])]});}
            var Q23;
            {var subQ0=sQuery(id+"F0.wireOp",EDGE,"E18");var subQ1=sQuery(id+"F0.wireOp",EDGE,"E3.3");var subQ2=makeQuery(id+"F0.imprint","INTERSECT",VERTEX,{"derivedFrom":[subQ1,subQ0]});Q23=makeQuery(id+"F0.imprint","IMPRINT",FACE,{"disambiguationData":[TD([[makeQuery(id+"F0.imprint","IMPRINT",EDGE,{"disambiguationData":[TD([[subQ2,-1.0]])],"derivedFrom":subQ1}),1.0]])]});}
            var Q24;
            {var subQ0=sQuery(id+"F0.wireOp",EDGE,"E18");var subQ1=sQuery(id+"F0.wireOp",EDGE,"E3.3");var subQ2=makeQuery(id+"F0.imprint","INTERSECT",VERTEX,{"derivedFrom":[subQ1,subQ0]});Q24=makeQuery(id+"F0.imprint","IMPRINT",FACE,{"disambiguationData":[TD([[makeQuery(id+"F0.imprint","IMPRINT",EDGE,{"disambiguationData":[TD([[subQ2,-1.0]])],"derivedFrom":subQ1}),-1.0]])]});}
            var Q25;
            {var subQ0=sQuery(id+"F0.wireOp",EDGE,"E18");var subQ1=sQuery(id+"F0.wireOp",EDGE,"E0.top");var subQ2=makeQuery(id+"F0.imprint","INTERSECT",VERTEX,{"derivedFrom":[subQ1,subQ0]});Q25=makeQuery(id+"F0.imprint","IMPRINT",FACE,{"disambiguationData":[TD([[makeQuery(id+"F0.imprint","IMPRINT",EDGE,{"disambiguationData":[TD([[subQ2,-1.0]])],"derivedFrom":subQ1}),-1.0]])]});}
            var Q26;
            {var subQ0=sQuery(id+"F0.wireOp",EDGE,"E20");var subQ1=sQuery(id+"F0.wireOp",EDGE,"E0.top");var subQ2=makeQuery(id+"F0.imprint","INTERSECT",VERTEX,{"derivedFrom":[subQ1,subQ0]});Q26=makeQuery(id+"F0.imprint","IMPRINT",FACE,{"disambiguationData":[TD([[makeQuery(id+"F0.imprint","IMPRINT",EDGE,{"disambiguationData":[TD([[subQ2,-1.0]])],"derivedFrom":subQ1}),-1.0]])]});}
            var Q27;
            {var subQ0=sQuery(id+"F0.wireOp",EDGE,"E20");var subQ1=sQuery(id+"F0.wireOp",EDGE,"E3.3");var subQ2=makeQuery(id+"F0.imprint","INTERSECT",VERTEX,{"derivedFrom":[subQ1,subQ0]});Q27=makeQuery(id+"F0.imprint","IMPRINT",FACE,{"disambiguationData":[TD([[makeQuery(id+"F0.imprint","IMPRINT",EDGE,{"disambiguationData":[TD([[subQ2,-1.0]])],"derivedFrom":subQ1}),-1.0]])]});}
            var Q28;
            {var subQ0=sQuery(id+"F0.wireOp",EDGE,"E20");var subQ1=sQuery(id+"F0.wireOp",EDGE,"E3.3");var subQ2=makeQuery(id+"F0.imprint","INTERSECT",VERTEX,{"derivedFrom":[subQ1,subQ0]});Q28=makeQuery(id+"F0.imprint","IMPRINT",FACE,{"disambiguationData":[TD([[makeQuery(id+"F0.imprint","IMPRINT",EDGE,{"disambiguationData":[TD([[subQ2,-1.0]])],"derivedFrom":subQ1}),1.0]])]});}
            var Q29;
            {var subQ0=sQuery(id+"F0.wireOp",EDGE,"E39.MirrorCS");var subQ1=sQuery(id+"F0.wireOp",EDGE,"E3.3");var subQ2=makeQuery(id+"F0.imprint","INTERSECT",VERTEX,{"derivedFrom":[subQ1,subQ0]});Q29=makeQuery(id+"F0.imprint","IMPRINT",FACE,{"disambiguationData":[TD([[makeQuery(id+"F0.imprint","IMPRINT",EDGE,{"disambiguationData":[TD([[subQ2,-1.0]])],"derivedFrom":subQ1}),1.0]])]});}
            var Q30;
            {var subQ0=sQuery(id+"F0.wireOp",EDGE,"E39.MirrorCS");var subQ1=sQuery(id+"F0.wireOp",EDGE,"E3.3");var subQ2=makeQuery(id+"F0.imprint","INTERSECT",VERTEX,{"derivedFrom":[subQ1,subQ0]});Q30=makeQuery(id+"F0.imprint","IMPRINT",FACE,{"disambiguationData":[TD([[makeQuery(id+"F0.imprint","IMPRINT",EDGE,{"disambiguationData":[TD([[subQ2,-1.0]])],"derivedFrom":subQ1}),-1.0]])]});}
            var Q31;
            {var subQ0=sQuery(id+"F0.wireOp",EDGE,"E39.MirrorCS");var subQ1=sQuery(id+"F0.wireOp",EDGE,"E0.top");var subQ2=makeQuery(id+"F0.imprint","INTERSECT",VERTEX,{"derivedFrom":[subQ1,subQ0]});Q31=makeQuery(id+"F0.imprint","IMPRINT",FACE,{"disambiguationData":[TD([[makeQuery(id+"F0.imprint","IMPRINT",EDGE,{"disambiguationData":[TD([[subQ2,-1.0]])],"derivedFrom":subQ1}),-1.0]])]});}
            var Q32;
            {var subQ0=sQuery(id+"F0.wireOp",EDGE,"E38.MirrorCS");var subQ1=sQuery(id+"F0.wireOp",EDGE,"E3.3");var subQ2=makeQuery(id+"F0.imprint","INTERSECT",VERTEX,{"derivedFrom":[subQ1,subQ0]});Q32=makeQuery(id+"F0.imprint","IMPRINT",FACE,{"disambiguationData":[TD([[makeQuery(id+"F0.imprint","IMPRINT",EDGE,{"disambiguationData":[TD([[subQ2,-1.0]])],"derivedFrom":subQ1}),1.0]])]});}
            var Q33;
            {var subQ0=sQuery(id+"F0.wireOp",EDGE,"E38.MirrorCS");var subQ1=sQuery(id+"F0.wireOp",EDGE,"E3.3");var subQ2=makeQuery(id+"F0.imprint","INTERSECT",VERTEX,{"derivedFrom":[subQ1,subQ0]});Q33=makeQuery(id+"F0.imprint","IMPRINT",FACE,{"disambiguationData":[TD([[makeQuery(id+"F0.imprint","IMPRINT",EDGE,{"disambiguationData":[TD([[subQ2,-1.0]])],"derivedFrom":subQ1}),-1.0]])]});}
            var Q34;
            {var subQ0=sQuery(id+"F0.wireOp",EDGE,"E38.MirrorCS");var subQ1=sQuery(id+"F0.wireOp",EDGE,"E0.top");var subQ2=makeQuery(id+"F0.imprint","INTERSECT",VERTEX,{"derivedFrom":[subQ1,subQ0]});Q34=makeQuery(id+"F0.imprint","IMPRINT",FACE,{"disambiguationData":[TD([[makeQuery(id+"F0.imprint","IMPRINT",EDGE,{"disambiguationData":[TD([[subQ2,-1.0]])],"derivedFrom":subQ1}),-1.0]])]});}
            var Q35;
            {var subQ0=sQuery(id+"F0.wireOp",EDGE,"E36.MirrorCS");var subQ1=sQuery(id+"F0.wireOp",EDGE,"E0.top");var subQ2=makeQuery(id+"F0.imprint","INTERSECT",VERTEX,{"derivedFrom":[subQ1,subQ0]});Q35=makeQuery(id+"F0.imprint","IMPRINT",FACE,{"disambiguationData":[TD([[makeQuery(id+"F0.imprint","IMPRINT",EDGE,{"disambiguationData":[TD([[subQ2,-1.0]])],"derivedFrom":subQ1}),-1.0]])]});}
            var Q36;
            {var subQ0=sQuery(id+"F0.wireOp",EDGE,"E36.MirrorCS");var subQ1=sQuery(id+"F0.wireOp",EDGE,"E3.3");var subQ2=makeQuery(id+"F0.imprint","INTERSECT",VERTEX,{"derivedFrom":[subQ1,subQ0]});Q36=makeQuery(id+"F0.imprint","IMPRINT",FACE,{"disambiguationData":[TD([[makeQuery(id+"F0.imprint","IMPRINT",EDGE,{"disambiguationData":[TD([[subQ2,-1.0]])],"derivedFrom":subQ1}),-1.0]])]});}
            var Q37;
            {var subQ0=sQuery(id+"F0.wireOp",EDGE,"E36.MirrorCS");var subQ1=sQuery(id+"F0.wireOp",EDGE,"E3.3");var subQ2=makeQuery(id+"F0.imprint","INTERSECT",VERTEX,{"derivedFrom":[subQ1,subQ0]});Q37=makeQuery(id+"F0.imprint","IMPRINT",FACE,{"disambiguationData":[TD([[makeQuery(id+"F0.imprint","IMPRINT",EDGE,{"disambiguationData":[TD([[subQ2,-1.0]])],"derivedFrom":subQ1}),1.0]])]});}
            var Q38;
            {var subQ0=sQuery(id+"F0.wireOp",EDGE,"E34.MirrorCS");var subQ1=sQuery(id+"F0.wireOp",EDGE,"E3.3");var subQ2=makeQuery(id+"F0.imprint","INTERSECT",VERTEX,{"derivedFrom":[subQ1,subQ0]});Q38=makeQuery(id+"F0.imprint","IMPRINT",FACE,{"disambiguationData":[TD([[makeQuery(id+"F0.imprint","IMPRINT",EDGE,{"disambiguationData":[TD([[subQ2,-1.0]])],"derivedFrom":subQ1}),1.0]])]});}
            var Q39;
            {var subQ0=sQuery(id+"F0.wireOp",EDGE,"E34.MirrorCS");var subQ1=sQuery(id+"F0.wireOp",EDGE,"E3.3");var subQ2=makeQuery(id+"F0.imprint","INTERSECT",VERTEX,{"derivedFrom":[subQ1,subQ0]});Q39=makeQuery(id+"F0.imprint","IMPRINT",FACE,{"disambiguationData":[TD([[makeQuery(id+"F0.imprint","IMPRINT",EDGE,{"disambiguationData":[TD([[subQ2,-1.0]])],"derivedFrom":subQ1}),-1.0]])]});}
            var Q40;
            {var subQ0=sQuery(id+"F0.wireOp",EDGE,"E34.MirrorCS");var subQ1=sQuery(id+"F0.wireOp",EDGE,"E0.top");var subQ2=makeQuery(id+"F0.imprint","INTERSECT",VERTEX,{"derivedFrom":[subQ1,subQ0]});Q40=makeQuery(id+"F0.imprint","IMPRINT",FACE,{"disambiguationData":[TD([[makeQuery(id+"F0.imprint","IMPRINT",EDGE,{"disambiguationData":[TD([[subQ2,-1.0]])],"derivedFrom":subQ1}),-1.0]])]});}
            var Q41;
            {var subQ0=sQuery(id+"F0.wireOp",EDGE,"E28.MirrorCS");var subQ1=sQuery(id+"F0.wireOp",EDGE,"E0.top");var subQ2=makeQuery(id+"F0.imprint","INTERSECT",VERTEX,{"derivedFrom":[subQ1,subQ0]});Q41=makeQuery(id+"F0.imprint","IMPRINT",FACE,{"disambiguationData":[TD([[makeQuery(id+"F0.imprint","IMPRINT",EDGE,{"disambiguationData":[TD([[subQ2,-1.0]])],"derivedFrom":subQ1}),-1.0]])]});}
            var Q42;
            {var subQ0=sQuery(id+"F0.wireOp",EDGE,"E28.MirrorCS");var subQ1=sQuery(id+"F0.wireOp",EDGE,"E3.3");var subQ2=makeQuery(id+"F0.imprint","INTERSECT",VERTEX,{"derivedFrom":[subQ1,subQ0]});Q42=makeQuery(id+"F0.imprint","IMPRINT",FACE,{"disambiguationData":[TD([[makeQuery(id+"F0.imprint","IMPRINT",EDGE,{"disambiguationData":[TD([[subQ2,-1.0]])],"derivedFrom":subQ1}),-1.0]])]});}
            var Q43;
            {var subQ0=sQuery(id+"F0.wireOp",EDGE,"E28.MirrorCS");var subQ1=sQuery(id+"F0.wireOp",EDGE,"E3.3");var subQ2=makeQuery(id+"F0.imprint","INTERSECT",VERTEX,{"derivedFrom":[subQ1,subQ0]});Q43=makeQuery(id+"F0.imprint","IMPRINT",FACE,{"disambiguationData":[TD([[makeQuery(id+"F0.imprint","IMPRINT",EDGE,{"disambiguationData":[TD([[subQ2,-1.0]])],"derivedFrom":subQ1}),1.0]])]});}
            var Q44;
            {var subQ0=sQuery(id+"F0.wireOp",EDGE,"E20");var subQ1=sQuery(id+"F0.wireOp",EDGE,"E4.top");var subQ2=makeQuery(id+"F0.imprint","INTERSECT",VERTEX,{"derivedFrom":[subQ1,subQ0]});Q44=makeQuery(id+"F0.imprint","IMPRINT",FACE,{"disambiguationData":[TD([[makeQuery(id+"F0.imprint","IMPRINT",EDGE,{"disambiguationData":[TD([[subQ2,-1.0]])],"derivedFrom":subQ1}),-1.0]])]});}
            var Q45;
            {var subQ0=sQuery(id+"F0.wireOp",EDGE,"E39.MirrorCS");var subQ1=sQuery(id+"F0.wireOp",EDGE,"E4.top");var subQ2=makeQuery(id+"F0.imprint","INTERSECT",VERTEX,{"derivedFrom":[subQ1,subQ0]});Q45=makeQuery(id+"F0.imprint","IMPRINT",FACE,{"disambiguationData":[TD([[makeQuery(id+"F0.imprint","IMPRINT",EDGE,{"disambiguationData":[TD([[subQ2,-1.0]])],"derivedFrom":subQ1}),-1.0]])]});}
            var Q46;
            {var subQ0=sQuery(id+"F0.wireOp",EDGE,"E20");var subQ1=sQuery(id+"F0.wireOp",EDGE,"E0.bottom");var subQ2=makeQuery(id+"F0.imprint","INTERSECT",VERTEX,{"derivedFrom":[subQ1,subQ0]});Q46=makeQuery(id+"F0.imprint","IMPRINT",FACE,{"disambiguationData":[TD([[makeQuery(id+"F0.imprint","IMPRINT",EDGE,{"disambiguationData":[TD([[subQ2,-1.0]])],"derivedFrom":subQ1}),1.0]])]});}
            var Q47;
            {var subQ1=sQuery(id+"F0.wireOp",EDGE,"E0.bottom");var subQ7=sQuery(id+"F0.wireOp",EDGE,"E39.MirrorCS");var subQ9=makeQuery(id+"F0.imprint","INTERSECT",VERTEX,{"derivedFrom":[subQ1,subQ7]});Q47=makeQuery(id+"F0.imprint","IMPRINT",FACE,{"disambiguationData":[TD([[makeQuery(id+"F0.imprint","IMPRINT",EDGE,{"disambiguationData":[TD([[subQ9,-1.0]])],"derivedFrom":subQ1}),1.0]])]});}
            var Q48;
            {var subQ0=sQuery(id+"F0.wireOp",EDGE,"E39.MirrorCS");var subQ1=sQuery(id+"F0.wireOp",EDGE,"E4.bottom");var subQ2=makeQuery(id+"F0.imprint","INTERSECT",VERTEX,{"derivedFrom":[subQ1,subQ0]});Q48=makeQuery(id+"F0.imprint","IMPRINT",FACE,{"disambiguationData":[TD([[makeQuery(id+"F0.imprint","IMPRINT",EDGE,{"disambiguationData":[TD([[subQ2,-1.0]])],"derivedFrom":subQ1}),-1.0]])]});}
            var Q49;
            {var subQ0=sQuery(id+"F0.wireOp",EDGE,"E39.MirrorCS");var subQ1=sQuery(id+"F0.wireOp",EDGE,"E0.bottom");var subQ2=makeQuery(id+"F0.imprint","INTERSECT",VERTEX,{"derivedFrom":[subQ1,subQ0]});Q49=makeQuery(id+"F0.imprint","IMPRINT",FACE,{"disambiguationData":[TD([[makeQuery(id+"F0.imprint","IMPRINT",EDGE,{"disambiguationData":[TD([[subQ2,-1.0]])],"derivedFrom":subQ1}),-1.0]])]});}
            var Q50;
            {var subQ0=sQuery(id+"F0.wireOp",EDGE,"E20");var subQ1=sQuery(id+"F0.wireOp",EDGE,"E4.bottom");var subQ2=makeQuery(id+"F0.imprint","INTERSECT",VERTEX,{"derivedFrom":[subQ1,subQ0]});Q50=makeQuery(id+"F0.imprint","IMPRINT",FACE,{"disambiguationData":[TD([[makeQuery(id+"F0.imprint","IMPRINT",EDGE,{"disambiguationData":[TD([[subQ2,-1.0]])],"derivedFrom":subQ1}),-1.0]])]});}
            var Q51;
            {var subQ0=sQuery(id+"F0.wireOp",EDGE,"E20");var subQ1=sQuery(id+"F0.wireOp",EDGE,"E0.bottom");var subQ2=makeQuery(id+"F0.imprint","INTERSECT",VERTEX,{"derivedFrom":[subQ1,subQ0]});Q51=makeQuery(id+"F0.imprint","IMPRINT",FACE,{"disambiguationData":[TD([[makeQuery(id+"F0.imprint","IMPRINT",EDGE,{"disambiguationData":[TD([[subQ2,-1.0]])],"derivedFrom":subQ1}),-1.0]])]});}
            var Q52;
            {var subQ0=sQuery(id+"F0.wireOp",EDGE,"E19");var subQ1=sQuery(id+"F0.wireOp",EDGE,"E2");var subQ2=makeQuery(id+"F0.imprint","INTERSECT",VERTEX,{"derivedFrom":[subQ1,subQ0]});Q52=makeQuery(id+"F0.imprint","IMPRINT",FACE,{"disambiguationData":[TD([[makeQuery(id+"F0.imprint","IMPRINT",EDGE,{"disambiguationData":[TD([[subQ2,1.0]])],"derivedFrom":subQ1}),-1.0]])]});}
            var Q53;
            {var subQ6=sQuery(id+"F0.wireOp",EDGE,"E2");var subQ9=sQuery(id+"F0.wireOp",EDGE,"E1");var subQ10=makeQuery(id+"F0.imprint","INTERSECT",VERTEX,{"derivedFrom":[subQ9,subQ6]});Q53=makeQuery(id+"F0.imprint","IMPRINT",FACE,{"disambiguationData":[TD([[makeQuery(id+"F0.imprint","IMPRINT",EDGE,{"disambiguationData":[TD([[subQ10,1.0]])],"derivedFrom":subQ9}),-1.0]])]});}
            var Q54;
            {var subQ0=sQuery(id+"F0.wireOp",EDGE,"E38.MirrorCS");var subQ1=sQuery(id+"F0.wireOp",EDGE,"E0.bottom");var subQ2=makeQuery(id+"F0.imprint","INTERSECT",VERTEX,{"derivedFrom":[subQ1,subQ0]});Q54=makeQuery(id+"F0.imprint","IMPRINT",FACE,{"disambiguationData":[TD([[makeQuery(id+"F0.imprint","IMPRINT",EDGE,{"disambiguationData":[TD([[subQ2,-1.0]])],"derivedFrom":subQ1}),1.0]])]});}
            var Q55;
            {var subQ0=sQuery(id+"F0.wireOp",EDGE,"E38.MirrorCS");var subQ1=sQuery(id+"F0.wireOp",EDGE,"E1");var subQ2=makeQuery(id+"F0.imprint","INTERSECT",VERTEX,{"derivedFrom":[subQ1,subQ0]});Q55=makeQuery(id+"F0.imprint","IMPRINT",FACE,{"disambiguationData":[TD([[makeQuery(id+"F0.imprint","IMPRINT",EDGE,{"disambiguationData":[TD([[subQ2,-1.0]])],"derivedFrom":subQ1}),-1.0]])]});}
            var Q56;
            {var subQ0=sQuery(id+"F0.wireOp",EDGE,"E38.MirrorCS");var subQ1=sQuery(id+"F0.wireOp",EDGE,"E0.bottom");var subQ2=makeQuery(id+"F0.imprint","INTERSECT",VERTEX,{"derivedFrom":[subQ1,subQ0]});Q56=makeQuery(id+"F0.imprint","IMPRINT",FACE,{"disambiguationData":[TD([[makeQuery(id+"F0.imprint","IMPRINT",EDGE,{"disambiguationData":[TD([[subQ2,-1.0]])],"derivedFrom":subQ1}),-1.0]])]});}
            var Q57;
            {var subQ0=sQuery(id+"F0.wireOp",EDGE,"E38.MirrorCS");var subQ1=sQuery(id+"F0.wireOp",EDGE,"E4.bottom");var subQ2=makeQuery(id+"F0.imprint","INTERSECT",VERTEX,{"derivedFrom":[subQ1,subQ0]});Q57=makeQuery(id+"F0.imprint","IMPRINT",FACE,{"disambiguationData":[TD([[makeQuery(id+"F0.imprint","IMPRINT",EDGE,{"disambiguationData":[TD([[subQ2,-1.0]])],"derivedFrom":subQ1}),-1.0]])]});}
            var Q58;
            {var subQ0=sQuery(id+"F0.wireOp",EDGE,"E36.MirrorCS");var subQ1=sQuery(id+"F0.wireOp",EDGE,"E4.bottom");var subQ2=makeQuery(id+"F0.imprint","INTERSECT",VERTEX,{"derivedFrom":[subQ1,subQ0]});Q58=makeQuery(id+"F0.imprint","IMPRINT",FACE,{"disambiguationData":[TD([[makeQuery(id+"F0.imprint","IMPRINT",EDGE,{"disambiguationData":[TD([[subQ2,-1.0]])],"derivedFrom":subQ1}),-1.0]])]});}
            var Q59;
            {var subQ0=sQuery(id+"F0.wireOp",EDGE,"E36.MirrorCS");var subQ1=sQuery(id+"F0.wireOp",EDGE,"E0.bottom");var subQ2=makeQuery(id+"F0.imprint","INTERSECT",VERTEX,{"derivedFrom":[subQ1,subQ0]});Q59=makeQuery(id+"F0.imprint","IMPRINT",FACE,{"disambiguationData":[TD([[makeQuery(id+"F0.imprint","IMPRINT",EDGE,{"disambiguationData":[TD([[subQ2,-1.0]])],"derivedFrom":subQ1}),-1.0]])]});}
            var Q60;
            {var subQ0=sQuery(id+"F0.wireOp",EDGE,"E36.MirrorCS");var subQ1=sQuery(id+"F0.wireOp",EDGE,"E0.bottom");var subQ2=makeQuery(id+"F0.imprint","INTERSECT",VERTEX,{"derivedFrom":[subQ1,subQ0]});Q60=makeQuery(id+"F0.imprint","IMPRINT",FACE,{"disambiguationData":[TD([[makeQuery(id+"F0.imprint","IMPRINT",EDGE,{"disambiguationData":[TD([[subQ2,-1.0]])],"derivedFrom":subQ1}),1.0]])]});}
            var Q61;
            {var subQ0=sQuery(id+"F0.wireOp",EDGE,"E36.MirrorCS");var subQ1=sQuery(id+"F0.wireOp",EDGE,"E1");var subQ2=makeQuery(id+"F0.imprint","INTERSECT",VERTEX,{"derivedFrom":[subQ1,subQ0]});Q61=makeQuery(id+"F0.imprint","IMPRINT",FACE,{"disambiguationData":[TD([[makeQuery(id+"F0.imprint","IMPRINT",EDGE,{"disambiguationData":[TD([[subQ2,-1.0]])],"derivedFrom":subQ1}),-1.0]])]});}
            var Q62;
            {var subQ0=sQuery(id+"F0.wireOp",EDGE,"E32.MirrorCS");Q62=makeQuery(id+"F0.imprint","IMPRINT",FACE,{"disambiguationData":[TD([[makeQuery(id+"F0.imprint","IMPRINT",EDGE,{"derivedFrom":subQ0}),-1.0]])]});}
            var Q63;
            {var subQ0=sQuery(id+"F0.wireOp",EDGE,"E34.MirrorCS");var subQ1=sQuery(id+"F0.wireOp",EDGE,"E0.bottom");var subQ2=makeQuery(id+"F0.imprint","INTERSECT",VERTEX,{"derivedFrom":[subQ1,subQ0]});Q63=makeQuery(id+"F0.imprint","IMPRINT",FACE,{"disambiguationData":[TD([[makeQuery(id+"F0.imprint","IMPRINT",EDGE,{"disambiguationData":[TD([[subQ2,-1.0]])],"derivedFrom":subQ1}),1.0]])]});}
            var Q64;
            {var subQ0=sQuery(id+"F0.wireOp",EDGE,"E34.MirrorCS");var subQ1=sQuery(id+"F0.wireOp",EDGE,"E0.bottom");var subQ2=makeQuery(id+"F0.imprint","INTERSECT",VERTEX,{"derivedFrom":[subQ1,subQ0]});Q64=makeQuery(id+"F0.imprint","IMPRINT",FACE,{"disambiguationData":[TD([[makeQuery(id+"F0.imprint","IMPRINT",EDGE,{"disambiguationData":[TD([[subQ2,-1.0]])],"derivedFrom":subQ1}),-1.0]])]});}
            var Q65;
            {var subQ1=sQuery(id+"F0.wireOp",EDGE,"E3.1");var subQ5=sQuery(id+"F0.wireOp",EDGE,"E0.bottom");var subQ6=makeQuery(id+"F0.imprint","INTERSECT",VERTEX,{"derivedFrom":[subQ5,subQ1]});Q65=makeQuery(id+"F0.imprint","IMPRINT",FACE,{"disambiguationData":[TD([[makeQuery(id+"F0.imprint","IMPRINT",EDGE,{"disambiguationData":[TD([[subQ6,-1.0]])],"derivedFrom":subQ5}),-1.0]])]});}
            var Q66;
            {var subQ0=sQuery(id+"F0.wireOp",EDGE,"E31.MirrorCS");Q66=makeQuery(id+"F0.imprint","IMPRINT",FACE,{"disambiguationData":[TD([[makeQuery(id+"F0.imprint","IMPRINT",EDGE,{"derivedFrom":subQ0}),1.0]])]});}
            var Q67;
            {var subQ0=sQuery(id+"F0.wireOp",EDGE,"E29.MirrorCS");var subQ1=sQuery(id+"F0.wireOp",EDGE,"E0.bottom");var subQ2=makeQuery(id+"F0.imprint","INTERSECT",VERTEX,{"derivedFrom":[subQ1,subQ0]});Q67=makeQuery(id+"F0.imprint","IMPRINT",FACE,{"disambiguationData":[TD([[makeQuery(id+"F0.imprint","IMPRINT",EDGE,{"disambiguationData":[TD([[subQ2,-1.0]])],"derivedFrom":subQ1}),-1.0]])]});}
            var Q68;
            {var subQ0=sQuery(id+"F0.wireOp",EDGE,"E3.1");var subQ1=sQuery(id+"F0.wireOp",EDGE,"E0.bottom");var subQ2=makeQuery(id+"F0.imprint","INTERSECT",VERTEX,{"derivedFrom":[subQ1,subQ0]});Q68=makeQuery(id+"F0.imprint","IMPRINT",FACE,{"disambiguationData":[TD([[makeQuery(id+"F0.imprint","IMPRINT",EDGE,{"disambiguationData":[TD([[subQ2,-1.0]])],"derivedFrom":subQ1}),1.0]])]});}
            var Q69;
            {var subQ0=sQuery(id+"F0.wireOp",EDGE,"E28.MirrorCS");var subQ1=sQuery(id+"F0.wireOp",EDGE,"E4.bottom");var subQ2=makeQuery(id+"F0.imprint","INTERSECT",VERTEX,{"derivedFrom":[subQ1,subQ0]});Q69=makeQuery(id+"F0.imprint","IMPRINT",FACE,{"disambiguationData":[TD([[makeQuery(id+"F0.imprint","IMPRINT",EDGE,{"disambiguationData":[TD([[subQ2,-1.0]])],"derivedFrom":subQ1}),-1.0]])]});}
            var Q70;
            {var subQ0=sQuery(id+"F0.wireOp",EDGE,"E34.MirrorCS");var subQ1=sQuery(id+"F0.wireOp",EDGE,"E4.bottom");var subQ2=makeQuery(id+"F0.imprint","INTERSECT",VERTEX,{"derivedFrom":[subQ1,subQ0]});Q70=makeQuery(id+"F0.imprint","IMPRINT",FACE,{"disambiguationData":[TD([[makeQuery(id+"F0.imprint","IMPRINT",EDGE,{"disambiguationData":[TD([[subQ2,-1.0]])],"derivedFrom":subQ1}),-1.0]])]});}
            extrude(context, id + "F2", {"entities" : qUnion([Q0, Q1, Q2, Q3, Q4, Q5, Q6, Q7, Q8, Q9, Q10, Q11, Q12, Q13, Q14, Q15, Q16, Q17, Q18, Q19, Q20, Q21, Q22, Q23, Q24, Q25, Q26, Q27, Q28, Q29, Q30, Q31, Q32, Q33, Q34, Q35, Q36, Q37, Q38, Q39, Q40, Q41, Q42, Q43, Q44, Q45, Q46, Q47, Q48, Q49, Q50, Q51, Q52, Q53, Q54, Q55, Q56, Q57, Q58, Q59, Q60, Q61, Q62, Q63, Q64, Q65, Q66, Q67, Q68, Q69, Q70]), "depth" : 23 * mm, "offsetDistance" : 25 * mm});
        }
    });
